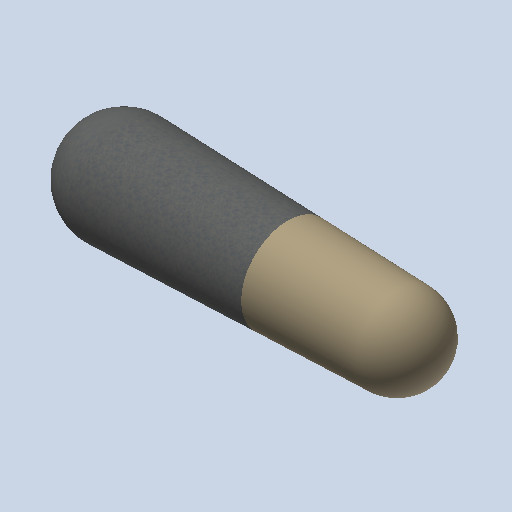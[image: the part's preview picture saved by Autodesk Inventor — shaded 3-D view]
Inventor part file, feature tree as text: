
AUTODESK INVENTOR PART (.ipt)
format: ipt  version: 2022 (Build 260153000, 153)  size: 215,552 bytes
history: native  units: mm (DEFAULTED — no unit token found)
features: other x1, revolve x1, plane x1, split x1, sketch x1
ambient origin geometry x8: Origin, YZ Plane, XZ Plane, XY Plane, X Axis, Y Axis, Z Axis, Center Point
bodies: Solid1 (feature_tree)
feature tree (5):
  other  "iMan - 2D BODY"
  revolve  "Revolution1"  [1 undecoded]
  plane  "Work Plane1"
  split  "Split1"
  sketch  "Sketch1"  dims[d1=10.0mm d16=279.4mm d17=106.426mm d18=88.138mm d19=90.0deg d20=-167.64mm]
note: 1 required parameter value undecoded (feature->parameter linkage not recoverable at this tier; creation-order binding heuristic only, values carry confidence <= 0.55)
